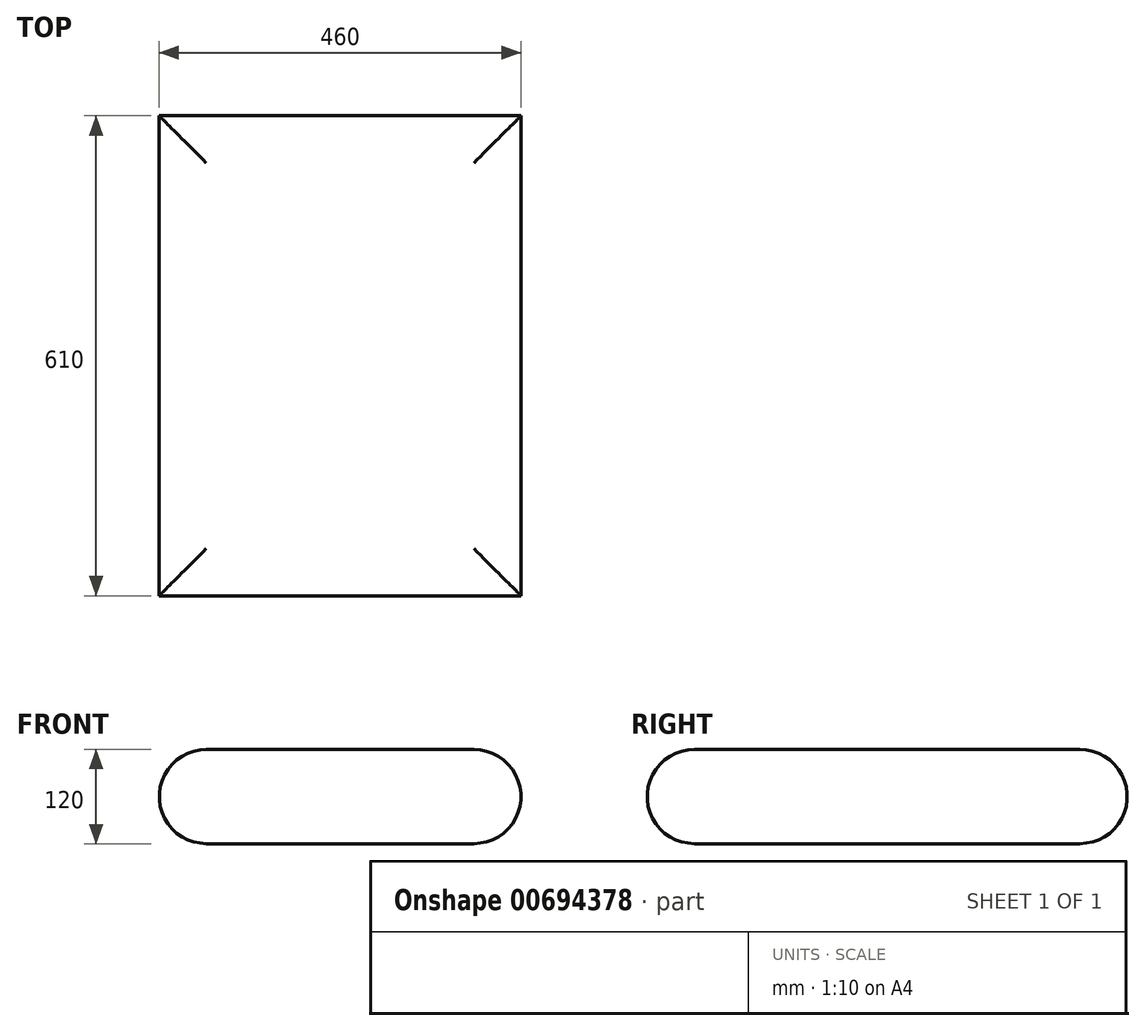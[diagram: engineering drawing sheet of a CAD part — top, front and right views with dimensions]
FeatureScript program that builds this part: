
annotation { "Feature Type Name" : "Feature", "Feature Type Description" : "" }
export const myFeature = defineFeature(function(context is Context, id is Id, definition is map)
    precondition{}
    {
        {
            var Q0;
            Q0=qCreatedBy(makeId("Front.planeOp"),FACE);
            var sketch = newSketch(context, id + "F0", { "sketchPlane" : qUnion([Q0])});
            skLineSegment(sketch, "E0", {"start": v(0, 0) * mm, "end": v(340, 0) * mm});
            skLineSegment(sketch, "E1", {"start": v(0, 120) * mm, "end": v(340, 120) * mm});
            skArc(sketch, "E2", {"start": v(0, 120) * mm, "mid": v(-60, 60) * mm, "end": v(0, 0) * mm});
            skArc(sketch, "E3", {"start": v(340, 0) * mm, "mid": v(400, 60) * mm, "end": v(340, 120) * mm});
            skSolve(sketch);
        }
        {
            var Q0;
            Q0 = qSketchRegion(id + "F0", true);
            extrude(context, id + "F1", {"entities" : qUnion([Q0]), "depth" : 610 * mm, "offsetDistance" : 25 * mm});
        }
        {
            var Q0;
            Q0=qCreatedBy(makeId("Right.planeOp"),FACE);
            var sketch = newSketch(context, id + "F2", { "sketchPlane" : qUnion([Q0])});
            skArc(sketch, "E4", {"start": v(-60, 0) * mm, "mid": v(0, 60) * mm, "end": v(-60, 120) * mm});
            skArc(sketch, "E5", {"start": v(-550, 120) * mm, "mid": v(-610, 60) * mm, "end": v(-550, 0) * mm});
            skLineSegment(sketch, "E6", {"start": v(-550, 120) * mm, "end": v(-550, 196.35) * mm});
            skLineSegment(sketch, "E7", {"start": v(-550, 196.35) * mm, "end": v(-774.31, 196.35) * mm});
            skLineSegment(sketch, "E8", {"start": v(-774.31, 196.35) * mm, "end": v(-774.31, -111.26) * mm});
            skLineSegment(sketch, "E9", {"start": v(-774.31, -111.26) * mm, "end": v(-538.92, -111.26) * mm});
            skLineSegment(sketch, "E10", {"start": v(-550, 0) * mm, "end": v(-511.02, -48.78) * mm});
            skLineSegment(sketch, "E11", {"start": v(-511.02, -48.78) * mm, "end": v(-61.06, -34.82) * mm});
            skLineSegment(sketch, "E12", {"start": v(-61.06, -34.82) * mm, "end": v(-60, 0) * mm});
            skLineSegment(sketch, "E13", {"start": v(-538.92, -111.26) * mm, "end": v(85.44, -111.26) * mm});
            skLineSegment(sketch, "E14", {"start": v(85.44, -111.26) * mm, "end": v(85.44, 155.2) * mm});
            skLineSegment(sketch, "E15", {"start": v(85.44, 155.2) * mm, "end": v(-27.93, 197.03) * mm});
            skLineSegment(sketch, "E16", {"start": v(-27.93, 197.03) * mm, "end": v(-60, 120) * mm});
            skSolve(sketch);
        }
        {
            var Q0;
            Q0 = qSketchRegion(id + "F2", true);
            extrude(context, id + "F3", {"entities" : qUnion([Q0]), "operationType" : NewBodyOperationType.REMOVE, "endBound" : BoundingType.SYMMETRIC, "depth" : 5000 * mm, "offsetDistance" : 25 * mm});
        }
    });
